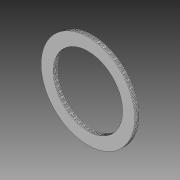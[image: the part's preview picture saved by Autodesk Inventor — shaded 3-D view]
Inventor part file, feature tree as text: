
AUTODESK INVENTOR PART (.ipt)
format: ipt  version: 2020 (Build 240168000, 168)  size: 526,336 bytes
history: native  units: mm
features: sketch x3, revolve x2, extrude x1, pattern_circular x1
ambient origin geometry x8: Origin, YZ Plane, XZ Plane, XY Plane, X Axis, Y Axis, Z Axis, Center Point
bodies: Solid1 (feature_tree)
feature tree (7):
  extrude  "Extrusion1"  Depth=100.0mm
  revolve  "Revolution1"  [1 undecoded]
  pattern_circular  "Circular Pattern1"  Count=50 Angle=360.0deg
  revolve  "Revolution2"  [1 undecoded]
  sketch  "Sketch1"  dims[d0=100.0mm d1=135.0mm]
  sketch  "Sketch2"  dims[d2=1.0mm d3=0.0mm d4=2.0mm]
  sketch  "Sketch3"  dims[d5=90.0deg d6=500.0mm d7=360.0deg d9=1.0mm d10=1.0mm d11=90.0deg]
note: 2 required parameter values undecoded (feature->parameter linkage not recoverable at this tier; creation-order binding heuristic only, values carry confidence <= 0.55)
